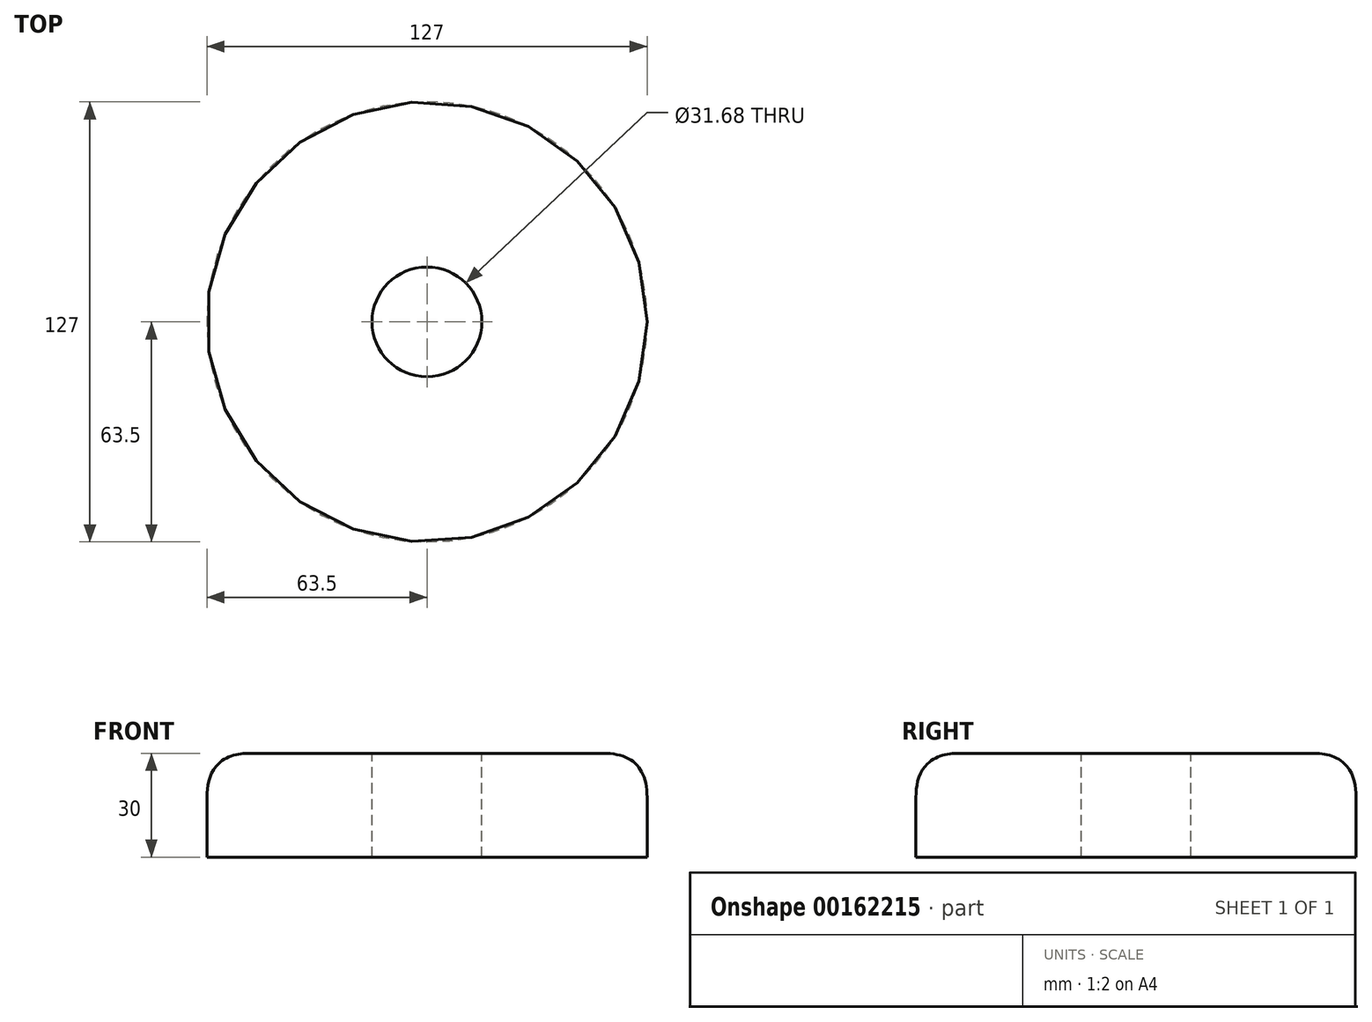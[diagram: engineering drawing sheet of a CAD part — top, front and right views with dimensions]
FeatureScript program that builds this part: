
annotation { "Feature Type Name" : "Feature", "Feature Type Description" : "" }
export const myFeature = defineFeature(function(context is Context, id is Id, definition is map)
    precondition{}
    {
        {
            var Q0;
            Q0=qCreatedBy(makeId("Top.planeOp"),FACE);
            var sketch = newSketch(context, id + "F0", { "sketchPlane" : qUnion([Q0])});
            skCircle(sketch, "E0", {"center": v(0, 0) * mm, "radius": 63.5 * mm});
            skSolve(sketch);
        }
        {
            var Q0;
            Q0 = qSketchRegion(id + "F0", true);
            extrude(context, id + "F1", {"entities" : qUnion([Q0]), "depth" : 30 * mm});
        }
        {
            var Q0;
            Q0=makeQuery(id+"F1.opExtrude","CAP_EDGE",EDGE,{"disambiguationData":[OSD([sQuery(id+"F0.wireOp",EDGE,"E0")])],"isStart":false});
            fillet(context, id + "F2", {"entities" : qUnion([Q0]), "radius" : 12.7 * mm, "tangentPropagation" : true, "rho" : 0.5, "crossSection" : FilletCrossSection.CONIC, "allowEdgeOverflow" : false});
        }
        {
            var Q0;
            Q0=makeQuery(id+"F1.opExtrude","CAP_FACE",FACE,{"disambiguationData":[OSD([sQuery(id+"F0.wireOp",EDGE,"E0")])],"isStart":false});
            var sketch = newSketch(context, id + "F3", { "sketchPlane" : qUnion([Q0])});
            skCircle(sketch, "E1", {"center": v(0, 0) * mm, "radius": 15.84 * mm});
            skSolve(sketch);
        }
        {
            var Q0;
            Q0=makeQuery(id+"F3.imprint","IMPRINT",FACE,{"disambiguationData":[TD([[makeQuery(id+"F3.imprint","IMPRINT",EDGE,{"derivedFrom":sQuery(id+"F3.wireOp",EDGE,"E1")}),1.0]])]});
            var Q1;
            Q1=makeQuery(id+"F1.opExtrude","SWEPT_BODY",BODY,{"disambiguationData":[OSD([sQuery(id+"F0.wireOp",EDGE,"E0")])]});
            extrude(context, id + "F4", {"entities" : qUnion([Q0]), "operationType" : NewBodyOperationType.REMOVE, "endBound" : BoundingType.UP_TO_BODY, "oppositeDirection" : true, "endBoundEntityBody" : qUnion([Q1]), "depth" : 25 * mm});
        }
    });
